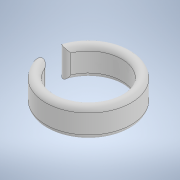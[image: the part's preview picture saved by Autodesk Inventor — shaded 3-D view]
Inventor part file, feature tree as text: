
AUTODESK INVENTOR PART (.ipt)
format: ipt  version: 2020 (Build 240168000, 168)  size: 163,840 bytes
history: native  units: in
note: dims shown in document units (in); Inventor stores cm internally (conversion verified against a paired STEP export)
features: extrude x1, fillet x1, sketch x1
ambient origin geometry x8: Origin, YZ Plane, XZ Plane, XY Plane, X Axis, Y Axis, Z Axis, Center Point
bodies: Solid1 (feature_tree)
feature tree (3):
  extrude  "Extrusion1"  Depth=0.0394in
  fillet  "Fillet1"  Radius=0.0984in
  sketch  "Sketch1"  dims[d0=0.5512in d1=0.7087in d2=0.0984in d3=0.0984in d4=0.2362in d5=0.0in d6=0.0394in]
